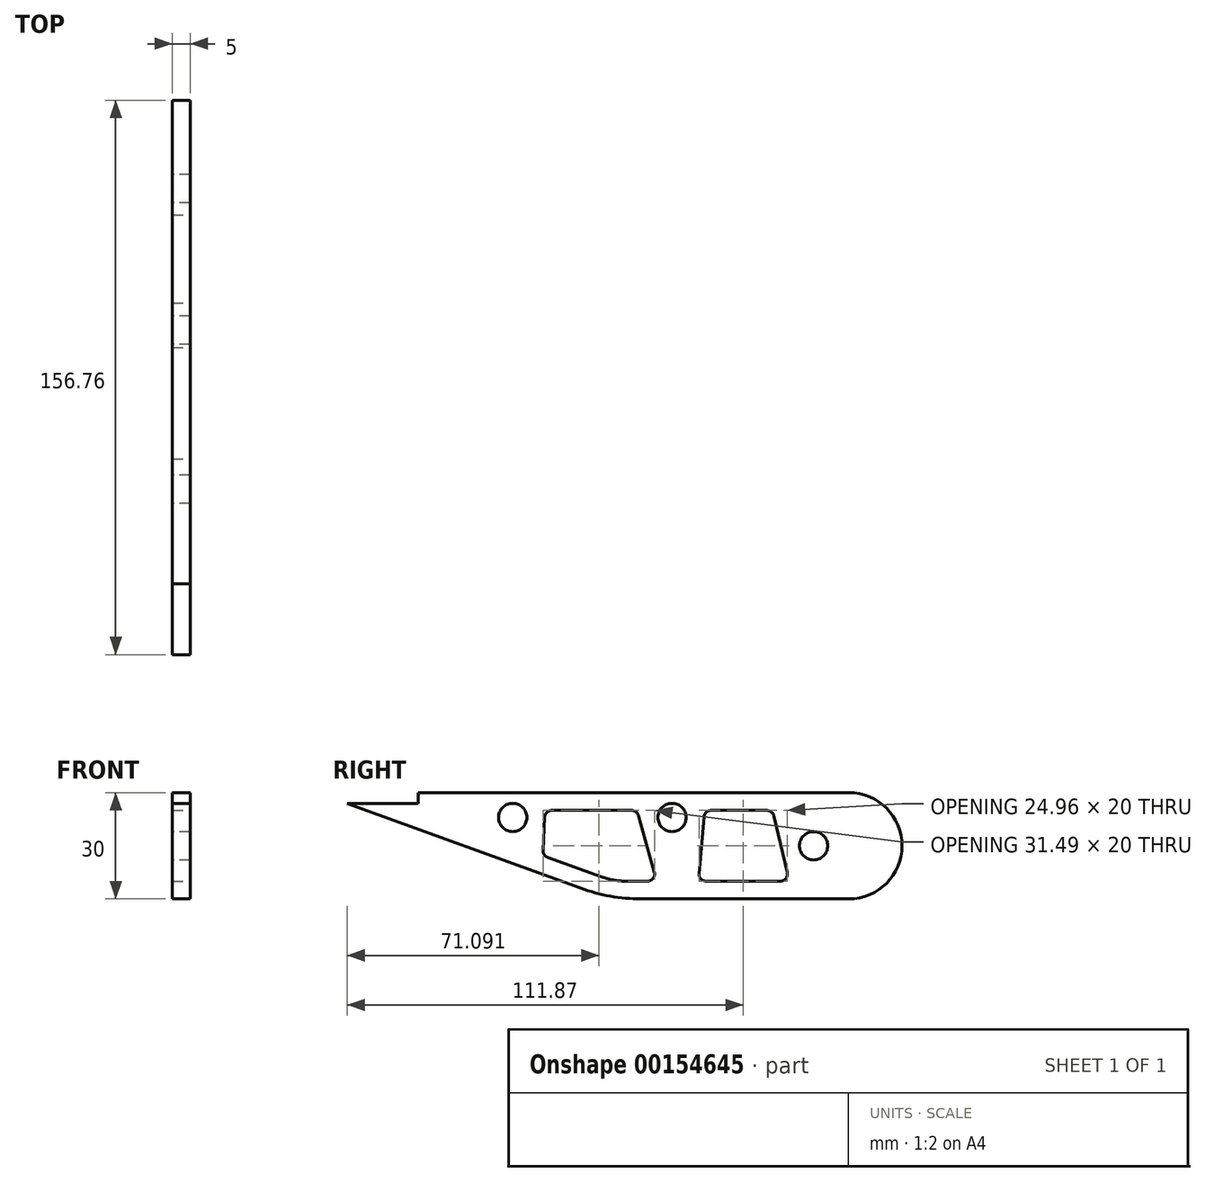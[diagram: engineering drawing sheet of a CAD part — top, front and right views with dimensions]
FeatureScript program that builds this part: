
annotation { "Feature Type Name" : "Feature", "Feature Type Description" : "" }
export const myFeature = defineFeature(function(context is Context, id is Id, definition is map)
    precondition{}
    {
        {
            var Q0;
            Q0=qCreatedBy(makeId("Right.planeOp"),FACE);
            var sketch = newSketch(context, id + "F0", { "sketchPlane" : qUnion([Q0])});
            skLineSegment(sketch, "E0.bottom", {"start": v(-71.76, 15) * mm, "end": v(50, 15) * mm});
            skLineSegment(sketch, "E0.top", {"start": v(-8.76, -15) * mm, "end": v(50, -15) * mm});
            skArc(sketch, "E1", {"start": v(50, -15) * mm, "mid": v(65, 0) * mm, "end": v(50, 15) * mm});
            skLineSegment(sketch, "E2", {"start": v(-91.76, 12) * mm, "end": v(-25.86, -11.98) * mm});
            skCircle(sketch, "E3", {"center": v(40, 0) * mm, "radius": 4 * mm});
            skPoint(sketch, "E4.visualSharp", {"position": v(-17.58, -15) * mm});
            skArc(sketch, "E4.filletArc", {"start": v(-25.86, -11.98) * mm, "mid": v(-17.44, -14.24) * mm, "end": v(-8.76, -15) * mm});
            skPoint(sketch, "E5.visualSharp", {"position": v(-100, 15) * mm});
            skCircle(sketch, "E6", {"center": v(0, 8) * mm, "radius": 4 * mm});
            skCircle(sketch, "E7", {"center": v(-45, 8) * mm, "radius": 4 * mm});
            skLineSegment(sketch, "E8.bottom", {"start": v(-71.76, 12) * mm, "end": v(-91.76, 12) * mm});
            skLineSegment(sketch, "E8.left", {"start": v(-71.76, 12) * mm, "end": v(-71.76, 15) * mm});
            skPoint(sketch, "E8.right.end.orphan", {"position": v(-105.69, 15) * mm});
            skSolve(sketch);
        }
        {
            var Q0;
            Q0=qSketchRegion(id+"F0",true);
            extrude(context, id + "F1", {"entities" : qUnion([Q0]), "depth" : 5 * mm});
        }
        {
            var Q0;
            Q0=makeQuery(id+"F1.opExtrude","CAP_FACE",FACE,{"disambiguationData":[OSD([sQuery(id+"F0.wireOp",EDGE,"E0.bottom"),sQuery(id+"F0.wireOp",EDGE,"E0.top"),sQuery(id+"F0.wireOp",EDGE,"E1"),sQuery(id+"F0.wireOp",EDGE,"E2"),sQuery(id+"F0.wireOp",EDGE,"E3"),sQuery(id+"F0.wireOp",EDGE,"E4.filletArc"),sQuery(id+"F0.wireOp",EDGE,"E5.filletArc"),sQuery(id+"F0.wireOp",EDGE,"E6"),sQuery(id+"F0.wireOp",EDGE,"E7")])],"isStart":false});
            var sketch = newSketch(context, id + "F2", { "sketchPlane" : qUnion([Q0])});
            skLineSegment(sketch, "E9", {"start": v(-33.99, 10) * mm, "end": v(-11.43, 10) * mm});
            skLineSegment(sketch, "E10", {"start": v(-9.5, 8.54) * mm, "end": v(-5, -7.46) * mm});
            skLineSegment(sketch, "E11", {"start": v(-6.92, -10) * mm, "end": v(-13.17, -10) * mm});
            skLineSegment(sketch, "E12", {"start": v(-20, -8.8) * mm, "end": v(-35.1, -3.3) * mm});
            skLineSegment(sketch, "E13", {"start": v(-36.41, -1.33) * mm, "end": v(-35.99, 8.1) * mm});
            skLineSegment(sketch, "E14", {"start": v(11.04, 10) * mm, "end": v(26.8, 10) * mm});
            skLineSegment(sketch, "E15", {"start": v(28.74, 8.46) * mm, "end": v(32.54, -7.54) * mm});
            skLineSegment(sketch, "E16", {"start": v(30.6, -10) * mm, "end": v(9.62, -10) * mm});
            skLineSegment(sketch, "E17", {"start": v(7.63, -7.82) * mm, "end": v(9.05, 8.18) * mm});
            skPoint(sketch, "E18.visualSharp", {"position": v(-16.7, -10) * mm});
            skArc(sketch, "E18.filletArc", {"start": v(-20, -8.8) * mm, "mid": v(-16.64, -9.7) * mm, "end": v(-13.17, -10) * mm});
            skPoint(sketch, "E19.visualSharp", {"position": v(-4.28, -10) * mm});
            skArc(sketch, "E19.filletArc", {"start": v(-6.92, -10) * mm, "mid": v(-5.33, -9.2) * mm, "end": v(-5, -7.46) * mm});
            skPoint(sketch, "E20.visualSharp", {"position": v(-9.91, 10) * mm});
            skArc(sketch, "E20.filletArc", {"start": v(-9.5, 8.54) * mm, "mid": v(-10.22, 9.6) * mm, "end": v(-11.43, 10) * mm});
            skPoint(sketch, "E21.visualSharp", {"position": v(-35.9, 10) * mm});
            skArc(sketch, "E21.filletArc", {"start": v(-33.99, 10) * mm, "mid": v(-35.37, 9.45) * mm, "end": v(-35.99, 8.1) * mm});
            skPoint(sketch, "E22.visualSharp", {"position": v(-36.48, -2.8) * mm});
            skArc(sketch, "E22.filletArc", {"start": v(-36.41, -1.33) * mm, "mid": v(-36.08, -2.53) * mm, "end": v(-35.1, -3.3) * mm});
            skPoint(sketch, "E23.visualSharp", {"position": v(7.44, -10) * mm});
            skArc(sketch, "E23.filletArc", {"start": v(7.63, -7.82) * mm, "mid": v(8.15, -9.35) * mm, "end": v(9.62, -10) * mm});
            skPoint(sketch, "E24.visualSharp", {"position": v(9.21, 10) * mm});
            skArc(sketch, "E24.filletArc", {"start": v(11.04, 10) * mm, "mid": v(9.7, 9.48) * mm, "end": v(9.05, 8.18) * mm});
            skPoint(sketch, "E25.visualSharp", {"position": v(28.38, 10) * mm});
            skArc(sketch, "E25.filletArc", {"start": v(28.74, 8.46) * mm, "mid": v(28.04, 9.57) * mm, "end": v(26.8, 10) * mm});
            skPoint(sketch, "E26.visualSharp", {"position": v(33.12, -10) * mm});
            skArc(sketch, "E26.filletArc", {"start": v(30.6, -10) * mm, "mid": v(32.16, -9.24) * mm, "end": v(32.54, -7.54) * mm});
            skPoint(sketch, "E27.visualSharp", {"position": v(49, 10) * mm});
            skPoint(sketch, "E28.visualSharp", {"position": v(49, -10) * mm});
            skPoint(sketch, "E29.orphan", {"position": v(50, 10) * mm});
            skSolve(sketch);
        }
        {
            var Q0;
            Q0 = qSketchRegion(id + "F2", true);
            extrude(context, id + "F3", {"entities" : qUnion([Q0]), "operationType" : NewBodyOperationType.REMOVE, "oppositeDirection" : true, "depth" : 25 * mm});
        }
    });
